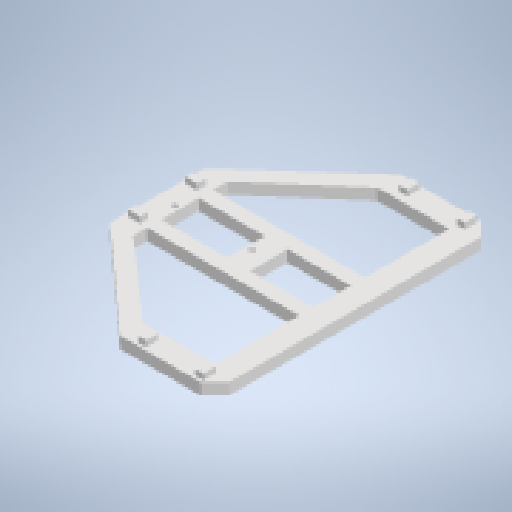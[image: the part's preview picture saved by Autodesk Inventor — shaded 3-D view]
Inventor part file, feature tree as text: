
AUTODESK INVENTOR PART (.ipt)
format: ipt  version: 2024.2 (Build 282272000, 272)  size: 354,304 bytes
history: native  units: mm
features: extrude x3, sketch x3, chamfer x1
ambient origin geometry x8: Origin, YZ Plane, XZ Plane, XY Plane, X Axis, Y Axis, Z Axis, Center Point
bodies: Solid1 (feature_tree)
feature tree (7):
  extrude  "Extrusion1"  Depth=5.0mm
  sketch  "Sketch4"  dims[d60=4.3mm d63=2.8mm]
  extrude  "Extrusion5"  Depth=2.8mm
  chamfer  "Chamfer6"  Distance=17.2mm
  extrude  "Extrusion7"  Depth=4.3mm
  sketch  "Sketch1"  dims[d18=4.0mm d19=0.0mm d57=5.0mm d58=5.0mm d59=33.0mm]
  sketch  "Sketch5"  dims[d64=2.8mm d66=17.2mm d67=4.3mm d68=1.1mm d78=2.0mm d79=0.0mm d85=33.0mm d95=8.0mm d97=97.7mm d99=59.5mm d100=8.0mm d102=69.0mm d103=8.0mm d104=13.0mm d105=23.0mm d106=13.0mm d112=8.0mm d113=8.0mm d114=8.0mm d115=8.0mm d119=8.0mm d120=13.0mm d122=8.0mm d133=5.1mm d134=1.1mm d135=5.0mm d136=2.0mm d137=45.0deg d138=5.0mm d139=5.0mm d141=5.0mm d142=2.0mm d143=2.0mm d144=2.0mm d145=2.0mm d146=6.5mm d147=6.5mm d148=9.0mm d149=0.0mm d150=4.3mm d151=2.8mm d152=4.3mm d153=2.8mm d154=17.2mm d155=1.1mm d156=5.1mm d157=5.0mm d158=48.85mm]
